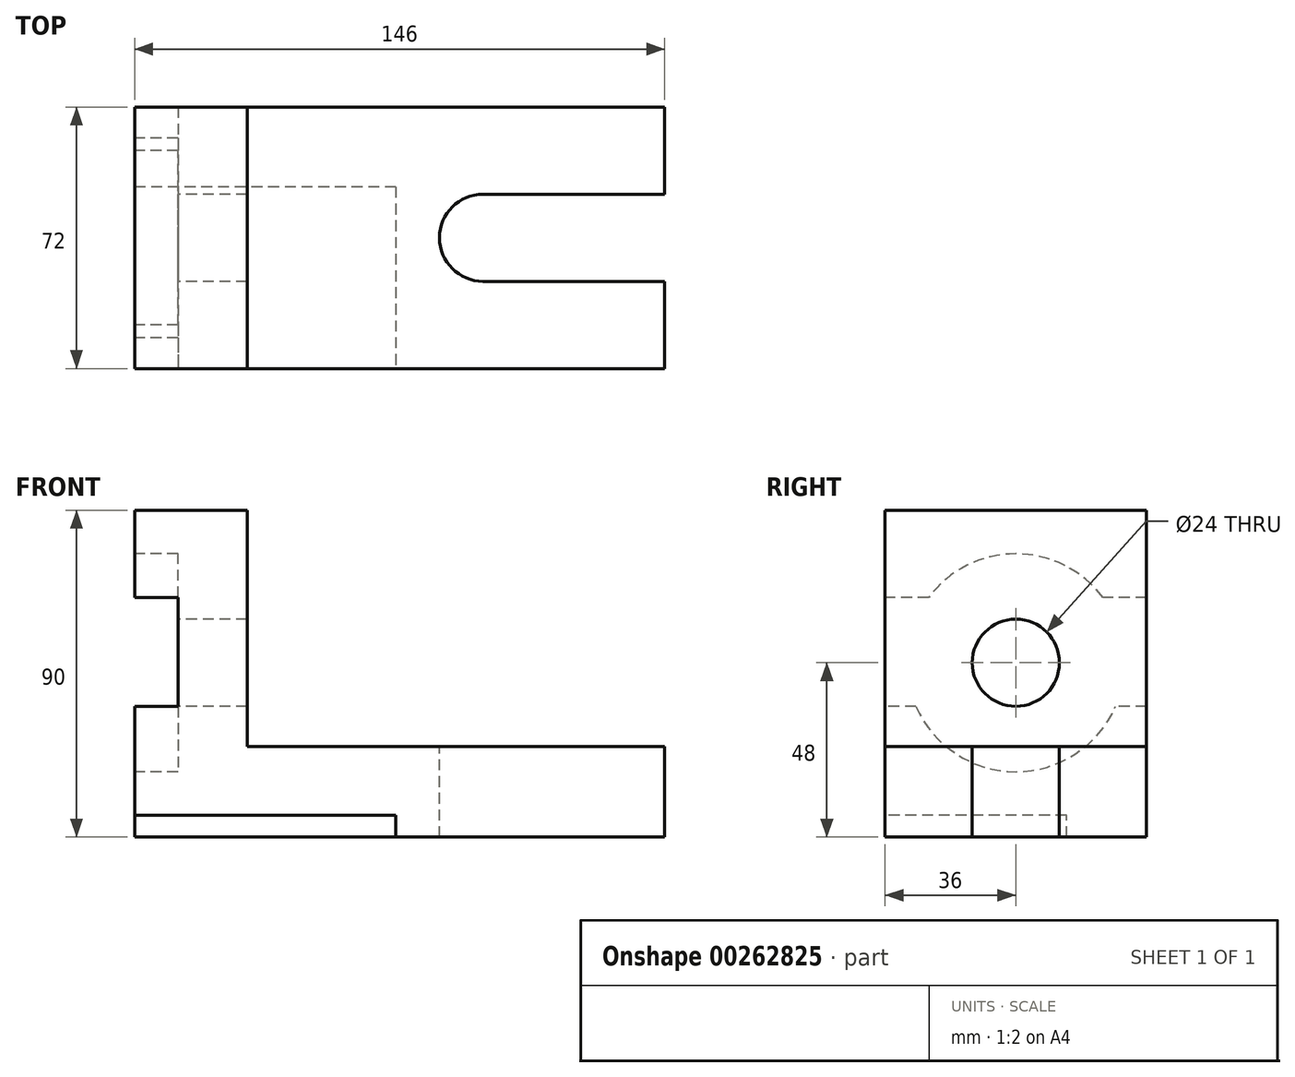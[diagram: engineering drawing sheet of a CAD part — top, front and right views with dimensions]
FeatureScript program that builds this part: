
annotation { "Feature Type Name" : "Feature", "Feature Type Description" : "" }
export const myFeature = defineFeature(function(context is Context, id is Id, definition is map)
    precondition{}
    {
        {
            var Q0;
            Q0=qCreatedBy(makeId("Front.planeOp"),FACE);
            var sketch = newSketch(context, id + "F0", { "sketchPlane" : qUnion([Q0])});
            skLineSegment(sketch, "E0", {"start": v(-146, 11) * mm, "end": v(-146, -19) * mm});
            skLineSegment(sketch, "E1", {"start": v(-146, -19) * mm, "end": v(-74, -19) * mm});
            skLineSegment(sketch, "E2", {"start": v(-74, -19) * mm, "end": v(-74, -25) * mm});
            skLineSegment(sketch, "E3", {"start": v(-74, -25) * mm, "end": v(0, -25) * mm});
            skLineSegment(sketch, "E4", {"start": v(0, -25) * mm, "end": v(0, 0) * mm});
            skLineSegment(sketch, "E5", {"start": v(-115, 0) * mm, "end": v(-115, 65) * mm});
            skLineSegment(sketch, "E6", {"start": v(-146, 11) * mm, "end": v(-134, 11) * mm});
            skLineSegment(sketch, "E7", {"start": v(-115, 0) * mm, "end": v(0, 0) * mm});
            skLineSegment(sketch, "E8", {"start": v(-134, 41) * mm, "end": v(-146, 41) * mm});
            skLineSegment(sketch, "E9", {"start": v(-134, 41) * mm, "end": v(-134, 11) * mm});
            skLineSegment(sketch, "E10", {"start": v(-146, 65) * mm, "end": v(-146, 41) * mm});
            skLineSegment(sketch, "E11", {"start": v(-146, 65) * mm, "end": v(-115, 65) * mm});
            skSolve(sketch);
        }
        {
            var Q0;
            Q0=qCreatedBy(makeId("Top.planeOp"),FACE);
            var sketch = newSketch(context, id + "F1", { "sketchPlane" : qUnion([Q0])});
            skLineSegment(sketch, "E12", {"start": v(-115, 0) * mm, "end": v(-115, 72) * mm});
            skLineSegment(sketch, "E13", {"start": v(-115, 72) * mm, "end": v(0, 72) * mm});
            skLineSegment(sketch, "E14", {"start": v(0, 72) * mm, "end": v(0, 0) * mm});
            skLineSegment(sketch, "E15", {"start": v(0, 0) * mm, "end": v(-115, 0) * mm});
            skSolve(sketch);
        }
        {
            var Q0;
            Q0=makeQuery(id+"F0.imprint","IMPRINT",FACE,{"disambiguationData":[TD([[makeQuery(id+"F0.imprint","IMPRINT",EDGE,{"derivedFrom":sQuery(id+"F0.wireOp",EDGE,"E0")}),1.0]])]});
            extrude(context, id + "F2", {"entities" : qUnion([Q0]), "oppositeDirection" : true, "depth" : 72 * mm});
        }
        {
            var Q0;
            Q0=makeQuery(id+"F2.opExtrude","SWEPT_FACE",FACE,{"disambiguationData":[OSD([sQuery(id+"F0.wireOp",EDGE,"E1")])]});
            var sketch = newSketch(context, id + "F3", { "sketchPlane" : qUnion([Q0])});
            skLineSegment(sketch, "E16.bottom", {"start": v(-74, -72) * mm, "end": v(-146, -72) * mm});
            skLineSegment(sketch, "E16.top", {"start": v(-74, -50) * mm, "end": v(-146, -50) * mm});
            skLineSegment(sketch, "E16.left", {"start": v(-74, -72) * mm, "end": v(-74, -50) * mm});
            skLineSegment(sketch, "E16.right", {"start": v(-146, -72) * mm, "end": v(-146, -50) * mm});
            skSolve(sketch);
        }
        {
            var Q0;
            Q0 = qSketchRegion(id + "F3", true);
            extrude(context, id + "F4", {"entities" : qUnion([Q0]), "operationType" : NewBodyOperationType.ADD, "depth" : 6 * mm});
        }
        {
            var Q0;
            Q0=qCreatedBy(makeId("Top.planeOp"),FACE);
            var sketch = newSketch(context, id + "F5", { "sketchPlane" : qUnion([Q0])});
            skLineSegment(sketch, "E17", {"start": v(0, 24) * mm, "end": v(-50, 24) * mm});
            skLineSegment(sketch, "E18", {"start": v(0, 24) * mm, "end": v(0, 48) * mm});
            skLineSegment(sketch, "E19", {"start": v(0, 48) * mm, "end": v(-50, 48) * mm});
            skArc(sketch, "E20", {"start": v(-50, 48) * mm, "mid": v(-62, 36) * mm, "end": v(-50, 24) * mm});
            skSolve(sketch);
        }
        {
            var Q0;
            Q0 = qSketchRegion(id + "F5", true);
            extrude(context, id + "F6", {"entities" : qUnion([Q0]), "operationType" : NewBodyOperationType.REMOVE, "endBound" : BoundingType.THROUGH_ALL, "oppositeDirection" : true, "depth" : 25 * mm});
        }
        {
            var Q0;
            Q0=makeQuery(id+"F4.boolean.opBoolean","MERGE",FACE,{"derivedFrom":[makeQuery(id+"F2.opExtrude","SWEPT_FACE",FACE,{"disambiguationData":[OSD([sQuery(id+"F0.wireOp",EDGE,"E0")])]}),makeQuery(id+"F4.opExtrude","SWEPT_FACE",FACE,{"disambiguationData":[OSD([sQuery(id+"F3.wireOp",EDGE,"E16.right")])]})]});
            var sketch = newSketch(context, id + "F7", { "sketchPlane" : qUnion([Q0])});
            skArc(sketch, "E21", {"start": v(-60, 13.25) * mm, "mid": v(-36, 1.25) * mm, "end": v(-12, 13.25) * mm});
            skLineSegment(sketch, "E22", {"start": v(-60, 13.25) * mm, "end": v(-12, 13.25) * mm});
            skSolve(sketch);
        }
        {
            var Q0;
            Q0=makeQuery(id+"F7.imprint","IMPRINT",FACE,{"disambiguationData":[TD([[makeQuery(id+"F7.imprint","IMPRINT",EDGE,{"derivedFrom":sQuery(id+"F7.wireOp",EDGE,"E21")}),1.0]])]});
            extrude(context, id + "F8", {"entities" : qUnion([Q0]), "operationType" : NewBodyOperationType.REMOVE, "oppositeDirection" : true, "depth" : 12 * mm});
        }
        {
            var Q0;
            Q0=makeQuery(id+"F2.opExtrude","SWEPT_FACE",FACE,{"disambiguationData":[OSD([sQuery(id+"F0.wireOp",EDGE,"E10")])]});
            var sketch = newSketch(context, id + "F9", { "sketchPlane" : qUnion([Q0])});
            skArc(sketch, "E23", {"start": v(-8.62, 35.25) * mm, "mid": v(-65.79, 19.42) * mm, "end": v(-6.5, 17.59) * mm});
            skLineSegment(sketch, "E24", {"start": v(-8.62, 35.25) * mm, "end": v(-6.5, 17.59) * mm});
            skSolve(sketch);
        }
        {
            var Q0;
            {var subQ0=sQuery(id+"F9.wireOp",EDGE,"E23");var subQ1=makeQuery(id+"F2.opExtrude","SWEPT_EDGE",EDGE,{"disambiguationData":[OSD([sQuery(id+"F0.wireOp",EDGE,"E8"),sQuery(id+"F0.wireOp",EDGE,"E10")])]});var subQ2=makeQuery(id+"F9.imprint","INTERSECT",VERTEX,{"disambiguationData":[OD(0.0)],"derivedFrom":[subQ1,subQ0]});Q0=makeQuery(id+"F9.imprint","IMPRINT",FACE,{"disambiguationData":[TD([[makeQuery(id+"F9.imprint","IMPRINT",EDGE,{"disambiguationData":[TD([[subQ2,-1.0]])],"derivedFrom":subQ0}),1.0]])]});}
            var Q1;
            {var subQ0=sQuery(id+"F9.wireOp",EDGE,"E24");Q1=makeQuery(id+"F9.imprint","IMPRINT",FACE,{"disambiguationData":[TD([[makeQuery(id+"F9.imprint","IMPRINT",EDGE,{"derivedFrom":subQ0}),-1.0]])]});}
            extrude(context, id + "F10", {"entities" : qUnion([Q0, Q1]), "operationType" : NewBodyOperationType.REMOVE, "oppositeDirection" : true, "depth" : 12 * mm});
        }
        {
            var Q0;
            Q0=makeQuery(id+"F10.boolean.opBoolean","MERGE",FACE,{"derivedFrom":[makeQuery(id+"F8.boolean.opBoolean","MERGE",FACE,{"derivedFrom":[makeQuery(id+"F2.opExtrude","SWEPT_FACE",FACE,{"disambiguationData":[OSD([sQuery(id+"F0.wireOp",EDGE,"E9")])]}),makeQuery(id+"F8.opExtrude","CAP_FACE",FACE,{"disambiguationData":[OSD([sQuery(id+"F7.wireOp",EDGE,"E21"),sQuery(id+"F7.wireOp",EDGE,"E22")])],"isStart":false})]}),makeQuery(id+"F10.opExtrude","CAP_FACE",FACE,{"disambiguationData":[OSD([sQuery(id+"F0.wireOp",EDGE,"E8"),sQuery(id+"F0.wireOp",EDGE,"E10"),sQuery(id+"F9.wireOp",EDGE,"E23")])],"isStart":false})]});
            var sketch = newSketch(context, id + "F11", { "sketchPlane" : qUnion([Q0])});
            skPoint(sketch, "E25.endSnap0", {"position": v(0, 26) * mm});
            skCircle(sketch, "E26", {"center": v(-36, 23) * mm, "radius": 12 * mm});
            skSolve(sketch);
        }
        {
            var Q0;
            Q0=makeQuery(id+"F11.imprint","IMPRINT",FACE,{"disambiguationData":[TD([[makeQuery(id+"F11.imprint","IMPRINT",EDGE,{"derivedFrom":sQuery(id+"F11.wireOp",EDGE,"E26")}),1.0]])]});
            extrude(context, id + "F12", {"entities" : qUnion([Q0]), "operationType" : NewBodyOperationType.REMOVE, "endBound" : BoundingType.THROUGH_ALL, "oppositeDirection" : true, "depth" : 25 * mm});
        }
    });
